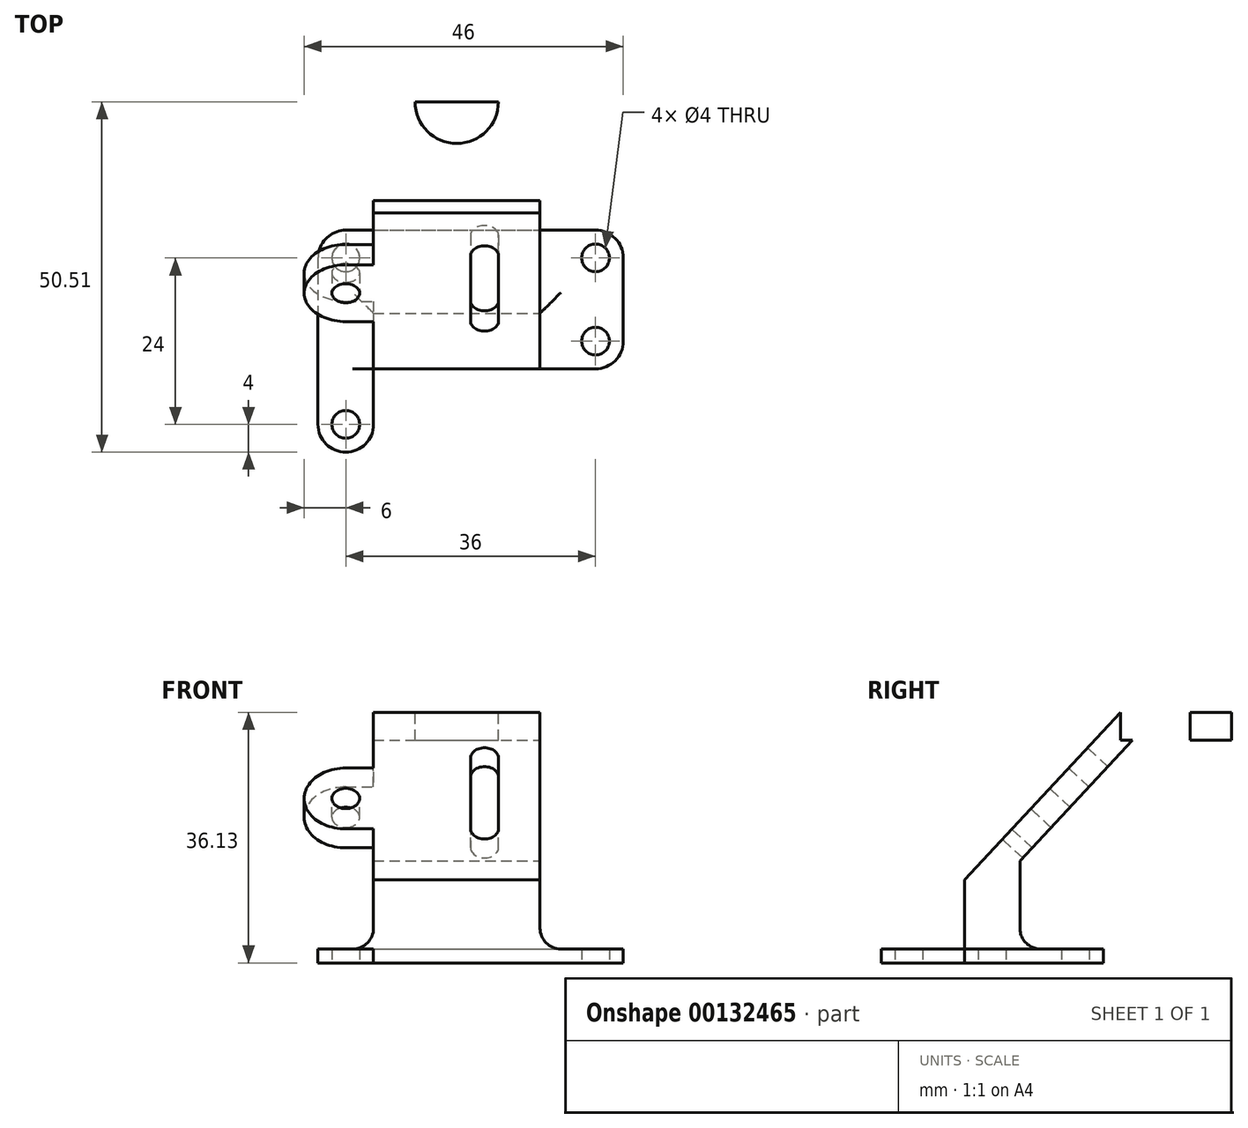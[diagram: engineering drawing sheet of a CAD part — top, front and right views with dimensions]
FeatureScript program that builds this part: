
annotation { "Feature Type Name" : "Feature", "Feature Type Description" : "" }
export const myFeature = defineFeature(function(context is Context, id is Id, definition is map)
    precondition{}
    {
        {
            var Q0;
            Q0=qCreatedBy(makeId("Top.planeOp"),FACE);
            var sketch = newSketch(context, id + "F0", { "sketchPlane" : qUnion([Q0])});
            skLineSegment(sketch, "E0", {"start": v(0, 0) * mm, "end": v(44, 0) * mm, "construction": true});
            skLineSegment(sketch, "E1", {"start": v(44, 0) * mm, "end": v(44, 20) * mm, "construction": true});
            skLineSegment(sketch, "E2", {"start": v(44, 20) * mm, "end": v(0, 20) * mm, "construction": true});
            skLineSegment(sketch, "E3", {"start": v(0, 20) * mm, "end": v(0, 0) * mm, "construction": true});
            skLineSegment(sketch, "E4", {"start": v(0, 20) * mm, "end": v(4, 20) * mm, "construction": true});
            skLineSegment(sketch, "E5", {"start": v(4, 20) * mm, "end": v(4, 16) * mm, "construction": true});
            skLineSegment(sketch, "E6", {"start": v(44, 20) * mm, "end": v(44, 16) * mm, "construction": true});
            skLineSegment(sketch, "E7", {"start": v(44, 16) * mm, "end": v(40, 16) * mm, "construction": true});
            skLineSegment(sketch, "E8", {"start": v(44, 0) * mm, "end": v(40, 0) * mm, "construction": true});
            skLineSegment(sketch, "E9", {"start": v(40, 0) * mm, "end": v(40, 4) * mm, "construction": true});
            skLineSegment(sketch, "E10", {"start": v(0, 0) * mm, "end": v(4, 0) * mm, "construction": true});
            skLineSegment(sketch, "E11", {"start": v(4, 0) * mm, "end": v(4, -8) * mm, "construction": true});
            skCircle(sketch, "E12", {"center": v(4, 16) * mm, "radius": 2 * mm});
            skArc(sketch, "E13", {"start": v(4, 20) * mm, "mid": v(1.17, 18.83) * mm, "end": v(0, 16) * mm});
            skCircle(sketch, "E14", {"center": v(4, -8) * mm, "radius": 2 * mm});
            skArc(sketch, "E15", {"start": v(0, -8) * mm, "mid": v(4, -12) * mm, "end": v(8, -8) * mm});
            skCircle(sketch, "E16", {"center": v(40, 4) * mm, "radius": 2 * mm});
            skArc(sketch, "E17", {"start": v(40, 0) * mm, "mid": v(42.83, 1.17) * mm, "end": v(44, 4) * mm});
            skCircle(sketch, "E18", {"center": v(40, 16) * mm, "radius": 2 * mm});
            skArc(sketch, "E19", {"start": v(44, 16) * mm, "mid": v(42.83, 18.83) * mm, "end": v(40, 20) * mm});
            skLineSegment(sketch, "E20", {"start": v(4, 20) * mm, "end": v(40, 20) * mm});
            skLineSegment(sketch, "E21", {"start": v(0, 16) * mm, "end": v(0, -8) * mm});
            skLineSegment(sketch, "E22", {"start": v(8, -8) * mm, "end": v(8, 0) * mm});
            skLineSegment(sketch, "E23", {"start": v(8, 0) * mm, "end": v(40, 0) * mm});
            skLineSegment(sketch, "E24", {"start": v(44, 4) * mm, "end": v(44, 16) * mm});
            skSolve(sketch);
        }
        {
            var Q0;
            Q0=makeQuery(id+"F0.imprint","IMPRINT",FACE,{"disambiguationData":[TD([[makeQuery(id+"F0.imprint","IMPRINT",EDGE,{"derivedFrom":sQuery(id+"F0.wireOp",EDGE,"E12")}),-1.0]])]});
            extrude(context, id + "F1", {"entities" : qUnion([Q0]), "depth" : 2 * mm});
        }
        {
            var Q0;
            Q0=makeQuery(id+"F1.opExtrude","CAP_FACE",FACE,{"disambiguationData":[OSD([sQuery(id+"F0.wireOp",EDGE,"E12"),sQuery(id+"F0.wireOp",EDGE,"E13"),sQuery(id+"F0.wireOp",EDGE,"E14"),sQuery(id+"F0.wireOp",EDGE,"E15"),sQuery(id+"F0.wireOp",EDGE,"E16"),sQuery(id+"F0.wireOp",EDGE,"E17"),sQuery(id+"F0.wireOp",EDGE,"E18"),sQuery(id+"F0.wireOp",EDGE,"E19"),sQuery(id+"F0.wireOp",EDGE,"E20"),sQuery(id+"F0.wireOp",EDGE,"E21"),sQuery(id+"F0.wireOp",EDGE,"E22"),sQuery(id+"F0.wireOp",EDGE,"E23"),sQuery(id+"F0.wireOp",EDGE,"E24")])],"isStart":false});
            var sketch = newSketch(context, id + "F2", { "sketchPlane" : qUnion([Q0])});
            skLineSegment(sketch, "E25", {"start": v(8, 0) * mm, "end": v(32, 0) * mm});
            skLineSegment(sketch, "E26", {"start": v(32, 0) * mm, "end": v(32, 8) * mm});
            skLineSegment(sketch, "E27", {"start": v(32, 8) * mm, "end": v(8, 8) * mm});
            skLineSegment(sketch, "E28", {"start": v(8, 8) * mm, "end": v(8, 0) * mm});
            skSolve(sketch);
        }
        {
            var Q0;
            Q0=makeQuery(id+"F2.imprint","IMPRINT",FACE,{"disambiguationData":[TD([[makeQuery(id+"F2.imprint","IMPRINT",EDGE,{"derivedFrom":sQuery(id+"F2.wireOp",EDGE,"E25")}),1.0]])]});
            extrude(context, id + "F3", {"entities" : qUnion([Q0]), "operationType" : NewBodyOperationType.ADD, "depth" : 10 * mm});
        }
        {
            var Q0;
            Q0=makeQuery(id+"F3.boolean.opBoolean","MERGE",FACE,{"derivedFrom":[makeQuery(id+"F1.opExtrude","SWEPT_FACE",FACE,{"disambiguationData":[OSD([sQuery(id+"F0.wireOp",EDGE,"E23")])]}),makeQuery(id+"F3.opExtrude","SWEPT_FACE",FACE,{"disambiguationData":[OSD([sQuery(id+"F2.wireOp",EDGE,"E25")])]})]});
            var sketch = newSketch(context, id + "F4", { "sketchPlane" : qUnion([Q0])});
            skLineSegment(sketch, "E29.0.0", {"start": v(0, 0) * mm, "end": v(8, 0) * mm});
            skLineSegment(sketch, "E29.0.1", {"start": v(8, 0) * mm, "end": v(8, 2) * mm});
            skLineSegment(sketch, "E29.0.2", {"start": v(8, 2) * mm, "end": v(0, 2) * mm});
            skLineSegment(sketch, "E29.0.3", {"start": v(0, 2) * mm, "end": v(0, 0) * mm});
            skArc(sketch, "E30", {"start": v(5, 2) * mm, "mid": v(7.12, 2.88) * mm, "end": v(8, 5) * mm});
            skLineSegment(sketch, "E31", {"start": v(5, 2) * mm, "end": v(8, 2) * mm});
            skArc(sketch, "E32", {"start": v(32, 5) * mm, "mid": v(32.88, 2.88) * mm, "end": v(35, 2) * mm});
            skLineSegment(sketch, "E33", {"start": v(35, 2) * mm, "end": v(32, 2) * mm});
            skLineSegment(sketch, "E34", {"start": v(32, 2) * mm, "end": v(32, 5) * mm});
            skSolve(sketch);
        }
        {
            var Q0;
            Q0=makeQuery(id+"F4.imprint","IMPRINT",FACE,{"disambiguationData":[TD([[makeQuery(id+"F4.imprint","IMPRINT",EDGE,{"derivedFrom":sQuery(id+"F4.wireOp",EDGE,"E32")}),-1.0]])]});
            var Q1;
            {var subQ0=sQuery(id+"F4.wireOp",EDGE,"E30");Q1=makeQuery(id+"F4.imprint","IMPRINT",FACE,{"disambiguationData":[TD([[makeQuery(id+"F4.imprint","IMPRINT",EDGE,{"derivedFrom":subQ0}),-1.0]])]});}
            extrude(context, id + "F5", {"entities" : qUnion([Q0, Q1]), "operationType" : NewBodyOperationType.ADD, "oppositeDirection" : true, "depth" : 8 * mm});
        }
        {
            var Q0;
            Q0=makeQuery(id+"F1.opExtrude","SWEPT_FACE",FACE,{"disambiguationData":[OSD([sQuery(id+"F0.wireOp",EDGE,"E24")])]});
            var sketch = newSketch(context, id + "F6", { "sketchPlane" : qUnion([Q0])});
            skLineSegment(sketch, "E35.0.0", {"start": v(0, 5) * mm, "end": v(0, 2) * mm});
            skLineSegment(sketch, "E35.0.1", {"start": v(0, 2) * mm, "end": v(8, 2) * mm});
            skLineSegment(sketch, "E35.0.2", {"start": v(8, 2) * mm, "end": v(8, 5) * mm});
            skLineSegment(sketch, "E35.0.3", {"start": v(8, 5) * mm, "end": v(0, 5) * mm});
            skLineSegment(sketch, "E36", {"start": v(8, 2) * mm, "end": v(11, 2) * mm});
            skArc(sketch, "E37", {"start": v(8, 5) * mm, "mid": v(8.88, 2.88) * mm, "end": v(11, 2) * mm});
            skSolve(sketch);
        }
        {
            var Q0;
            Q0=makeQuery(id+"F6.imprint","IMPRINT",FACE,{"disambiguationData":[TD([[makeQuery(id+"F6.imprint","IMPRINT",EDGE,{"derivedFrom":sQuery(id+"F6.wireOp",EDGE,"E35.0.2")}),-1.0]])]});
            extrude(context, id + "F7", {"entities" : qUnion([Q0]), "operationType" : NewBodyOperationType.ADD, "oppositeDirection" : true, "depth" : 40 * mm});
        }
        {
            var Q0;
            {var subQ0=sQuery(id+"F2.wireOp",EDGE,"E25");Q0=makeQuery(id+"F5.boolean.opBoolean","MERGE",FACE,{"derivedFrom":[makeQuery(id+"F3.boolean.opBoolean","MERGE",FACE,{"derivedFrom":[makeQuery(id+"F1.opExtrude","SWEPT_FACE",FACE,{"disambiguationData":[OSD([sQuery(id+"F0.wireOp",EDGE,"E23")])]}),makeQuery(id+"F3.opExtrude","SWEPT_FACE",FACE,{"disambiguationData":[OSD([subQ0])]})]}),makeQuery(id+"F5.opExtrude","CAP_FACE",FACE,{"disambiguationData":[OSD([sQuery(id+"F0.wireOp",EDGE,"E22"),subQ0,sQuery(id+"F2.wireOp",EDGE,"E28"),sQuery(id+"F4.wireOp",EDGE,"E30"),sQuery(id+"F4.wireOp",EDGE,"E31")])],"isStart":true}),makeQuery(id+"F5.opExtrude","CAP_FACE",FACE,{"disambiguationData":[OSD([sQuery(id+"F4.wireOp",EDGE,"E32"),sQuery(id+"F4.wireOp",EDGE,"E33"),sQuery(id+"F4.wireOp",EDGE,"E34")])],"isStart":true})]});}
            var sketch = newSketch(context, id + "F8", { "sketchPlane" : qUnion([Q0])});
            skArc(sketch, "E38", {"start": v(32, 5) * mm, "mid": v(32.88, 2.88) * mm, "end": v(35, 2) * mm});
            skLineSegment(sketch, "E39", {"start": v(32, 5) * mm, "end": v(44, 5) * mm});
            skLineSegment(sketch, "E40", {"start": v(44, 5) * mm, "end": v(44, 2) * mm});
            skLineSegment(sketch, "E41", {"start": v(44, 2) * mm, "end": v(35, 2) * mm});
            skLineSegment(sketch, "E42", {"start": v(5, 2) * mm, "end": v(3.85, 2) * mm});
            skLineSegment(sketch, "E43", {"start": v(3.85, 2) * mm, "end": v(3.85, 5) * mm});
            skLineSegment(sketch, "E44", {"start": v(3.85, 5) * mm, "end": v(8, 5) * mm});
            skSolve(sketch);
        }
        {
            var Q0;
            Q0=makeQuery(id+"F8.imprint","IMPRINT",FACE,{"disambiguationData":[TD([[makeQuery(id+"F8.imprint","IMPRINT",EDGE,{"derivedFrom":sQuery(id+"F8.wireOp",EDGE,"E42")}),-1.0]])]});
            var Q1;
            {var subQ3=sQuery(id+"F8.wireOp",EDGE,"E38");Q1=makeQuery(id+"F8.imprint","IMPRINT",FACE,{"disambiguationData":[TD([[makeQuery(id+"F8.imprint","IMPRINT",EDGE,{"derivedFrom":subQ3}),1.0]])]});}
            extrude(context, id + "F9", {"entities" : qUnion([Q0, Q1]), "operationType" : NewBodyOperationType.REMOVE, "oppositeDirection" : true, "depth" : 25 * mm});
        }
        {
            var Q0;
            Q0=makeQuery(id+"F3.opExtrude","SWEPT_FACE",FACE,{"disambiguationData":[OSD([sQuery(id+"F2.wireOp",EDGE,"E26")])]});
            var sketch = newSketch(context, id + "F10", { "sketchPlane" : qUnion([Q0])});
            skLineSegment(sketch, "E45", {"start": v(0, 12) * mm, "end": v(22.5, 36.13) * mm});
            skLineSegment(sketch, "E46", {"start": v(24.25, 32.13) * mm, "end": v(8, 14.71) * mm});
            skLineSegment(sketch, "E47", {"start": v(8, 12) * mm, "end": v(8, 14.71) * mm});
            skLineSegment(sketch, "E48", {"start": v(22.5, 36.13) * mm, "end": v(38.5, 36.13) * mm});
            skLineSegment(sketch, "E49", {"start": v(38.5, 36.13) * mm, "end": v(38.5, 32.13) * mm});
            skLineSegment(sketch, "E50", {"start": v(38.5, 32.13) * mm, "end": v(24.25, 32.13) * mm});
            skSolve(sketch);
        }
        {
            var Q0;
            Q0=makeQuery(id+"F10.imprint","IMPRINT",FACE,{"disambiguationData":[TD([[makeQuery(id+"F10.imprint","IMPRINT",EDGE,{"derivedFrom":sQuery(id+"F10.wireOp",EDGE,"E45")}),-1.0]])]});
            extrude(context, id + "F11", {"entities" : qUnion([Q0]), "operationType" : NewBodyOperationType.ADD, "oppositeDirection" : true, "depth" : 24 * mm});
        }
        {
            var Q0;
            Q0=makeQuery(id+"F11.opExtrude","SWEPT_FACE",FACE,{"disambiguationData":[OSD([sQuery(id+"F10.wireOp",EDGE,"E45")])]});
            var sketch = newSketch(context, id + "F12", { "sketchPlane" : qUnion([Q0])});
            skLineSegment(sketch, "E51", {"start": v(32, 41.78) * mm, "end": v(24, 41.78) * mm, "construction": true});
            skLineSegment(sketch, "E52", {"start": v(24, 41.78) * mm, "end": v(24, 32.78) * mm, "construction": true});
            skLineSegment(sketch, "E53", {"start": v(24, 32.78) * mm, "end": v(24, 18.78) * mm, "construction": true});
            skLineSegment(sketch, "E54", {"start": v(24, 32.78) * mm, "end": v(22, 32.78) * mm, "construction": true});
            skLineSegment(sketch, "E55", {"start": v(24, 32.78) * mm, "end": v(26, 32.78) * mm, "construction": true});
            skLineSegment(sketch, "E56", {"start": v(22, 18.78) * mm, "end": v(24, 18.78) * mm, "construction": true});
            skLineSegment(sketch, "E57", {"start": v(24, 18.78) * mm, "end": v(26, 18.78) * mm, "construction": true});
            skArc(sketch, "E58", {"start": v(26, 32.78) * mm, "mid": v(24, 34.78) * mm, "end": v(22, 32.78) * mm});
            skArc(sketch, "E59", {"start": v(22, 18.78) * mm, "mid": v(24, 16.78) * mm, "end": v(26, 18.78) * mm});
            skLineSegment(sketch, "E60", {"start": v(22, 32.78) * mm, "end": v(22, 18.78) * mm});
            skLineSegment(sketch, "E61", {"start": v(26, 18.78) * mm, "end": v(26, 32.78) * mm});
            skSolve(sketch);
        }
        {
            var Q0;
            Q0=makeQuery(id+"F12.imprint","IMPRINT",FACE,{"disambiguationData":[TD([[makeQuery(id+"F12.imprint","IMPRINT",EDGE,{"derivedFrom":sQuery(id+"F12.wireOp",EDGE,"E58")}),1.0]])]});
            extrude(context, id + "F13", {"entities" : qUnion([Q0]), "operationType" : NewBodyOperationType.REMOVE, "oppositeDirection" : true, "depth" : 4 * mm});
        }
        {
            var Q0;
            Q0=makeQuery(id+"F11.opExtrude","SWEPT_FACE",FACE,{"disambiguationData":[OSD([sQuery(id+"F10.wireOp",EDGE,"E45")])]});
            var sketch = newSketch(context, id + "F14", { "sketchPlane" : qUnion([Q0])});
            skLineSegment(sketch, "E62", {"start": v(8, 41.78) * mm, "end": v(8, 24.78) * mm, "construction": true});
            skLineSegment(sketch, "E63", {"start": v(8, 24.78) * mm, "end": v(4, 24.78) * mm, "construction": true});
            skCircle(sketch, "E64", {"center": v(4, 24.78) * mm, "radius": 2 * mm});
            skArc(sketch, "E65", {"start": v(4, 30.78) * mm, "mid": v(-2, 24.78) * mm, "end": v(4, 18.78) * mm});
            skLineSegment(sketch, "E66", {"start": v(4, 24.78) * mm, "end": v(4, 30.78) * mm, "construction": true});
            skLineSegment(sketch, "E67", {"start": v(4, 30.78) * mm, "end": v(4, 18.78) * mm, "construction": true});
            skLineSegment(sketch, "E68", {"start": v(4, 18.78) * mm, "end": v(8, 18.78) * mm});
            skLineSegment(sketch, "E69", {"start": v(4, 30.78) * mm, "end": v(8, 30.78) * mm});
            skSolve(sketch);
        }
        {
            var Q0;
            Q0=makeQuery(id+"F14.imprint","IMPRINT",FACE,{"disambiguationData":[TD([[makeQuery(id+"F14.imprint","IMPRINT",EDGE,{"derivedFrom":sQuery(id+"F14.wireOp",EDGE,"E64")}),-1.0]])]});
            extrude(context, id + "F15", {"entities" : qUnion([Q0]), "operationType" : NewBodyOperationType.ADD, "oppositeDirection" : true, "depth" : 4 * mm});
        }
        {
            var Q0;
            Q0=makeQuery(id+"F11.opExtrude","SWEPT_FACE",FACE,{"disambiguationData":[OSD([sQuery(id+"F10.wireOp",EDGE,"E48")])]});
            var sketch = newSketch(context, id + "F16", { "sketchPlane" : qUnion([Q0])});
            skArc(sketch, "E70", {"start": v(26, 38.5) * mm, "mid": v(20, 32.5) * mm, "end": v(14, 38.5) * mm});
            skLineSegment(sketch, "E71", {"start": v(14, 38.5) * mm, "end": v(26, 38.5) * mm});
            skSolve(sketch);
        }
        {
            var Q0;
            Q0=makeQuery(id+"F16.imprint","IMPRINT",FACE,{"disambiguationData":[TD([[makeQuery(id+"F16.imprint","IMPRINT",EDGE,{"derivedFrom":sQuery(id+"F16.wireOp",EDGE,"E70")}),-1.0]])]});
            extrude(context, id + "F17", {"entities" : qUnion([Q0]), "operationType" : NewBodyOperationType.REMOVE, "oppositeDirection" : true, "depth" : 4 * mm});
        }
    });
